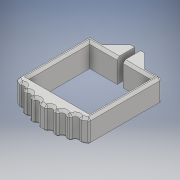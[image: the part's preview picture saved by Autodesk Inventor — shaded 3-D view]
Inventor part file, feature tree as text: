
AUTODESK INVENTOR PART (.ipt)
format: ipt  version: 2018 (Build 220112000, 112)  size: 292,864 bytes
history: native  units: mm
features: extrude x5, sketch x5, mirror x2, chamfer x2, fillet x1, projected_geometry x1
ambient origin geometry x8: Origin, YZ Plane, XZ Plane, XY Plane, X Axis, Y Axis, Z Axis, Center Point
bodies: Solid1 (feature_tree)
feature tree (16):
  extrude  "Extrusion1"  TaperAngle=135.0deg  [1 undecoded]
  extrude  "Extrusion2"  Depth=15.0mm
  extrude  "Extrusion3"  Depth=5.0mm
  mirror  "Mirror1"
  extrude  "Extrusion4"  Depth=5.0mm
  extrude  "Extrusion5"  Depth=20.0mm TaperAngle=0.0deg
  mirror  "Mirror2"
  fillet  "Fillet1"  Radius=5.0mm
  chamfer  "Chamfer1"  Distance=20.0mm
  chamfer  "Chamfer2"  Distance=12.0mm
  sketch  "Sketch2"  dims[d2=52.0mm d3=135.0deg]
  sketch  "Sketch4"  dims[d4=135.0deg d5=15.0mm]
  projected_geometry  "Projected Loop1"
  sketch  "Sketch6"  dims[d6=5.0mm d7=5.0mm]
  sketch  "Sketch7"  dims[d9=12.0mm d10=5.0mm]
  sketch  "Sketch8"  dims[d11=10.0mm d12=20.0mm d13=0.0mm d14=5.0mm d15=20.0mm d16=0.0mm d17=12.0mm d18=0.0mm d19=4.5mm d20=17.453293mm d21=10.0mm d22=0.0mm d23=5.0mm d24=9.0mm d25=9.0mm d26=9.0mm d28=10.0mm d29=0.0mm d30=2.0mm d31=2.0mm d32=2.0mm d33=45.0deg d34=2.0mm d35=2.0mm d36=45.0deg]
note: 1 required parameter value undecoded (feature->parameter linkage not recoverable at this tier; creation-order binding heuristic only, values carry confidence <= 0.55)
